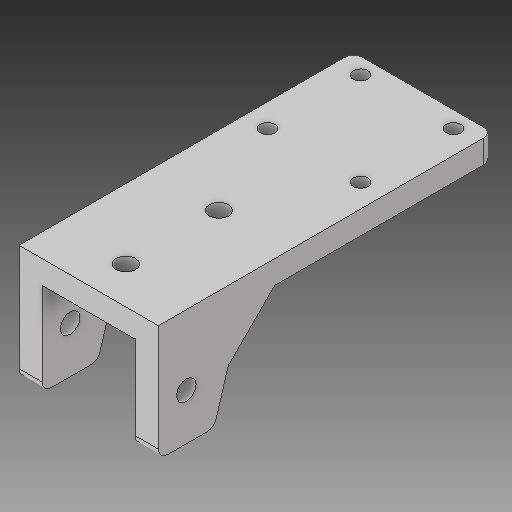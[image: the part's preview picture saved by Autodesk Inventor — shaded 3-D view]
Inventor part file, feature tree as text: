
AUTODESK INVENTOR PART (.ipt)
format: ipt  version: 2018 (Build 220112000, 112)  size: 140,288 bytes
history: native  units: in
note: dims shown in document units (in); Inventor stores cm internally (conversion verified against a paired STEP export)
features: sketch x4, other x3
ambient origin geometry x8: Origin, YZ Plane, XZ Plane, XY Plane, X Axis, Y Axis, Z Axis, Center Point
bodies: Solid1 (feature_tree)
feature tree (7):
  other  "X-connector-left.ipt"
  other  "Solid1::X-connector-left.ipt"
  other  "TaggingFeature1"
  sketch  "Sketch1"  dims[d0=0.3937in]
  sketch  "Sketch2"
  sketch  "Sketch3"
  sketch  "Sketch4"
